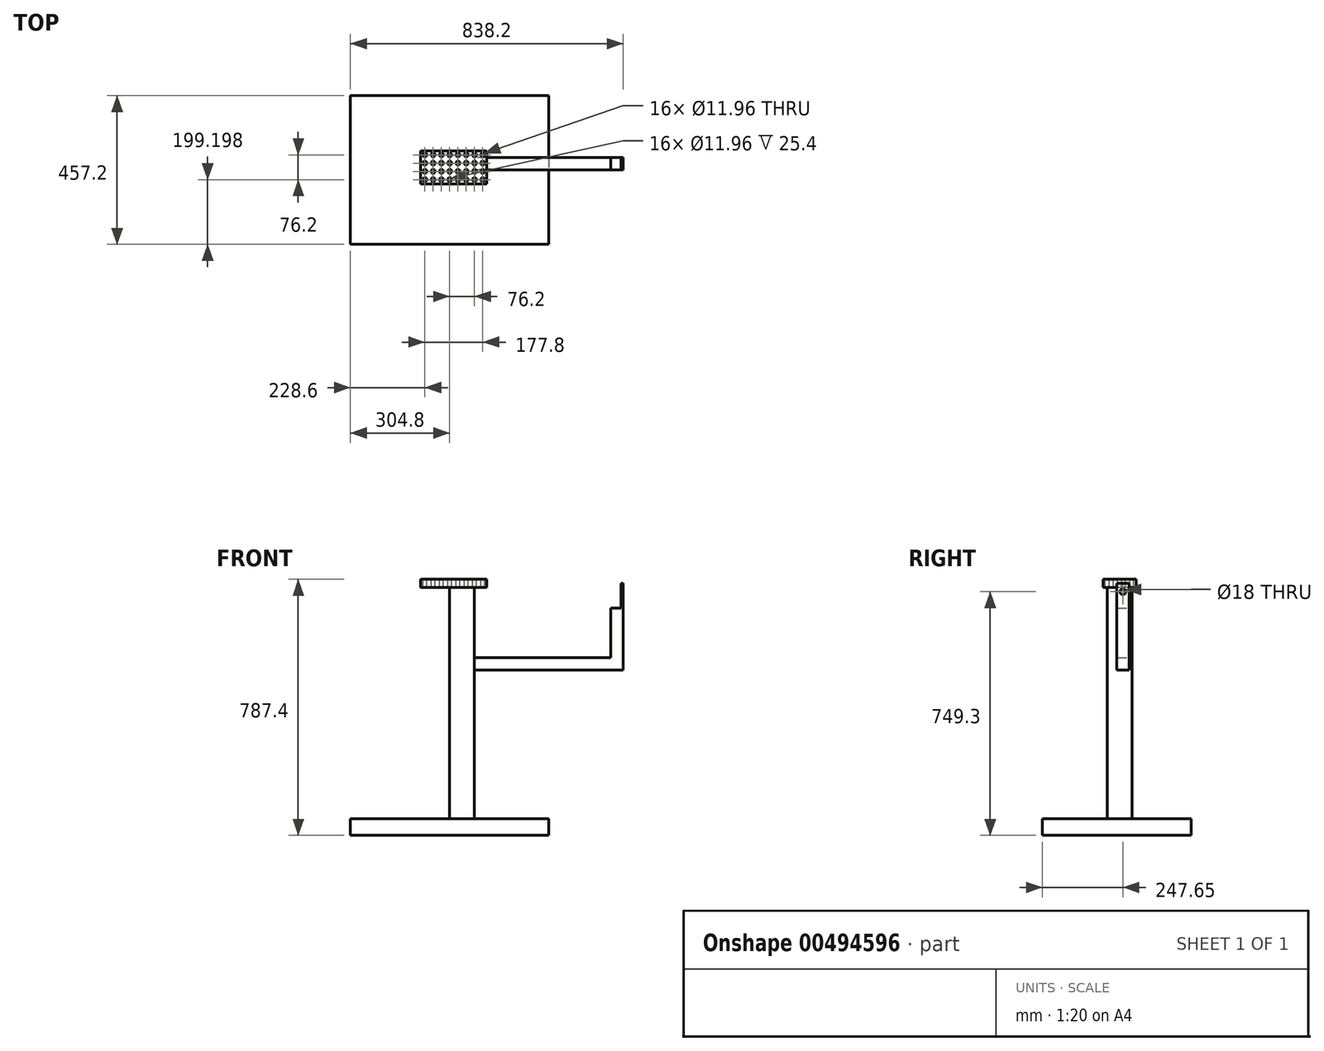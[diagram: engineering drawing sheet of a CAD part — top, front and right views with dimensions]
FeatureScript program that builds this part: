
annotation { "Feature Type Name" : "Feature", "Feature Type Description" : "" }
export const myFeature = defineFeature(function(context is Context, id is Id, definition is map)
    precondition{}
    {
        {
            var Q0;
            Q0=qCreatedBy(makeId("Top.planeOp"),FACE);
            var sketch = newSketch(context, id + "F0", { "sketchPlane" : qUnion([Q0])});
            skLineSegment(sketch, "E0.bottom", {"start": v(-304.8, 228.6) * mm, "end": v(304.8, 228.6) * mm});
            skLineSegment(sketch, "E0.top", {"start": v(-304.8, -228.6) * mm, "end": v(304.8, -228.6) * mm});
            skLineSegment(sketch, "E0.left", {"start": v(-304.8, 228.6) * mm, "end": v(-304.8, -228.6) * mm});
            skLineSegment(sketch, "E0.right", {"start": v(304.8, 228.6) * mm, "end": v(304.8, -228.6) * mm});
            skSolve(sketch);
        }
        {
            var Q0;
            Q0 = qSketchRegion(id + "F0", true);
            extrude(context, id + "F1", {"entities" : qUnion([Q0]), "depth" : 50.8 * mm});
        }
        {
            var Q0;
            Q0=makeQuery(id+"F1.opExtrude","CAP_FACE",FACE,{"disambiguationData":[OSD([sQuery(id+"F0.wireOp",EDGE,"E0.bottom"),sQuery(id+"F0.wireOp",EDGE,"E0.top"),sQuery(id+"F0.wireOp",EDGE,"E0.left"),sQuery(id+"F0.wireOp",EDGE,"E0.right")])],"isStart":false});
            var sketch = newSketch(context, id + "F2", { "sketchPlane" : qUnion([Q0])});
            skLineSegment(sketch, "E1.bottom", {"start": v(0, 46.8) * mm, "end": v(76.2, 46.8) * mm});
            skLineSegment(sketch, "E1.top", {"start": v(0, -29.4) * mm, "end": v(76.2, -29.4) * mm});
            skLineSegment(sketch, "E1.left", {"start": v(0, 46.8) * mm, "end": v(0, -29.4) * mm});
            skLineSegment(sketch, "E1.right", {"start": v(76.2, 46.8) * mm, "end": v(76.2, -29.4) * mm});
            skSolve(sketch);
        }
        {
            var Q0;
            Q0 = qSketchRegion(id + "F2", true);
            extrude(context, id + "F3", {"entities" : qUnion([Q0]), "operationType" : NewBodyOperationType.ADD, "depth" : 711.2 * mm});
        }
        {
            var Q0;
            Q0=makeQuery(id+"F3.opExtrude","CAP_FACE",FACE,{"disambiguationData":[OSD([sQuery(id+"F2.wireOp",EDGE,"E1.bottom"),sQuery(id+"F2.wireOp",EDGE,"E1.top"),sQuery(id+"F2.wireOp",EDGE,"E1.left"),sQuery(id+"F2.wireOp",EDGE,"E1.right")])],"isStart":false});
            var sketch = newSketch(context, id + "F4", { "sketchPlane" : qUnion([Q0])});
            skLineSegment(sketch, "E2.bottom", {"start": v(-88.9, 59.5) * mm, "end": v(114.3, 59.5) * mm});
            skLineSegment(sketch, "E2.top", {"start": v(-88.9, -42.1) * mm, "end": v(114.3, -42.1) * mm});
            skLineSegment(sketch, "E2.left", {"start": v(-88.9, 59.5) * mm, "end": v(-88.9, -42.1) * mm});
            skLineSegment(sketch, "E2.right", {"start": v(114.3, 59.5) * mm, "end": v(114.3, -42.1) * mm});
            skSolve(sketch);
        }
        {
            var Q0;
            Q0 = qSketchRegion(id + "F4", true);
            extrude(context, id + "F5", {"entities" : qUnion([Q0]), "operationType" : NewBodyOperationType.ADD, "depth" : 25.4 * mm});
        }
        {
            var Q0;
            Q0=makeQuery(id+"F5.opExtrude","CAP_FACE",FACE,{"disambiguationData":[OSD([sQuery(id+"F4.wireOp",EDGE,"E2.bottom"),sQuery(id+"F4.wireOp",EDGE,"E2.top"),sQuery(id+"F4.wireOp",EDGE,"E2.left"),sQuery(id+"F4.wireOp",EDGE,"E2.right")])],"isStart":false});
            var sketch = newSketch(context, id + "F6", { "sketchPlane" : qUnion([Q0])});
            skCircle(sketch, "E3", {"center": v(-76.2, 46.8) * mm, "radius": 5.98 * mm});
            skCircle(sketch, "E4.0.1.0", {"center": v(-76.2, 21.4) * mm, "radius": 5.98 * mm});
            skCircle(sketch, "E4.0.2.0", {"center": v(-76.2, -4) * mm, "radius": 5.98 * mm});
            skCircle(sketch, "E4.0.3.0", {"center": v(-76.2, -29.4) * mm, "radius": 5.98 * mm});
            skCircle(sketch, "E4.1.0.0", {"center": v(-50.8, 46.8) * mm, "radius": 5.98 * mm});
            skCircle(sketch, "E4.1.1.0", {"center": v(-50.8, 21.4) * mm, "radius": 5.98 * mm});
            skCircle(sketch, "E4.1.2.0", {"center": v(-50.8, -4) * mm, "radius": 5.98 * mm});
            skCircle(sketch, "E4.1.3.0", {"center": v(-50.8, -29.4) * mm, "radius": 5.98 * mm});
            skCircle(sketch, "E4.2.0.0", {"center": v(-25.4, 46.8) * mm, "radius": 5.98 * mm});
            skCircle(sketch, "E4.2.1.0", {"center": v(-25.4, 21.4) * mm, "radius": 5.98 * mm});
            skCircle(sketch, "E4.2.2.0", {"center": v(-25.4, -4) * mm, "radius": 5.98 * mm});
            skCircle(sketch, "E4.2.3.0", {"center": v(-25.4, -29.4) * mm, "radius": 5.98 * mm});
            skCircle(sketch, "E4.3.0.0", {"center": v(0, 46.8) * mm, "radius": 5.98 * mm});
            skCircle(sketch, "E4.3.1.0", {"center": v(0, 21.4) * mm, "radius": 5.98 * mm});
            skCircle(sketch, "E4.3.2.0", {"center": v(0, -4) * mm, "radius": 5.98 * mm});
            skCircle(sketch, "E4.3.3.0", {"center": v(0, -29.4) * mm, "radius": 5.98 * mm});
            skCircle(sketch, "E4.4.0.0", {"center": v(25.4, 46.8) * mm, "radius": 5.98 * mm});
            skCircle(sketch, "E4.4.1.0", {"center": v(25.4, 21.4) * mm, "radius": 5.98 * mm});
            skCircle(sketch, "E4.4.2.0", {"center": v(25.4, -4) * mm, "radius": 5.98 * mm});
            skCircle(sketch, "E4.4.3.0", {"center": v(25.4, -29.4) * mm, "radius": 5.98 * mm});
            skCircle(sketch, "E4.5.0.0", {"center": v(50.8, 46.8) * mm, "radius": 5.98 * mm});
            skCircle(sketch, "E4.5.1.0", {"center": v(50.8, 21.4) * mm, "radius": 5.98 * mm});
            skCircle(sketch, "E4.5.2.0", {"center": v(50.8, -4) * mm, "radius": 5.98 * mm});
            skCircle(sketch, "E4.5.3.0", {"center": v(50.8, -29.4) * mm, "radius": 5.98 * mm});
            skCircle(sketch, "E4.6.0.0", {"center": v(76.2, 46.8) * mm, "radius": 5.98 * mm});
            skCircle(sketch, "E4.6.1.0", {"center": v(76.2, 21.4) * mm, "radius": 5.98 * mm});
            skCircle(sketch, "E4.6.2.0", {"center": v(76.2, -4) * mm, "radius": 5.98 * mm});
            skCircle(sketch, "E4.6.3.0", {"center": v(76.2, -29.4) * mm, "radius": 5.98 * mm});
            skCircle(sketch, "E4.7.0.0", {"center": v(101.6, 46.8) * mm, "radius": 5.98 * mm});
            skCircle(sketch, "E4.7.1.0", {"center": v(101.6, 21.4) * mm, "radius": 5.98 * mm});
            skCircle(sketch, "E4.7.2.0", {"center": v(101.6, -4) * mm, "radius": 5.98 * mm});
            skCircle(sketch, "E4.7.3.0", {"center": v(101.6, -29.4) * mm, "radius": 5.98 * mm});
            skLineSegment(sketch, "E4.direction1", {"start": v(-76.2, 46.8) * mm, "end": v(-50.8, 46.8) * mm, "construction": true});
            skLineSegment(sketch, "E4.direction2", {"start": v(-76.2, 46.8) * mm, "end": v(-76.2, 21.4) * mm, "construction": true});
            skSolve(sketch);
        }
        {
            var Q0;
            Q0 = qSketchRegion(id + "F6", true);
            extrude(context, id + "F7", {"entities" : qUnion([Q0]), "operationType" : NewBodyOperationType.REMOVE, "oppositeDirection" : true, "depth" : 25.4 * mm});
        }
        {
            var Q0;
            Q0=makeQuery(id+"F3.opExtrude","SWEPT_FACE",FACE,{"disambiguationData":[OSD([sQuery(id+"F2.wireOp",EDGE,"E1.right")])]});
            var sketch = newSketch(context, id + "F8", { "sketchPlane" : qUnion([Q0])});
            skLineSegment(sketch, "E5.bottom", {"start": v(0, 546.1) * mm, "end": v(38.1, 546.1) * mm});
            skLineSegment(sketch, "E5.top", {"start": v(0, 508) * mm, "end": v(38.1, 508) * mm});
            skLineSegment(sketch, "E5.left", {"start": v(0, 546.1) * mm, "end": v(0, 508) * mm});
            skLineSegment(sketch, "E5.right", {"start": v(38.1, 546.1) * mm, "end": v(38.1, 508) * mm});
            skSolve(sketch);
        }
        {
            var Q0;
            Q0 = qSketchRegion(id + "F8", true);
            extrude(context, id + "F9", {"entities" : qUnion([Q0]), "operationType" : NewBodyOperationType.ADD, "depth" : 457.2 * mm});
        }
        {
            var Q0;
            Q0=makeQuery(id+"F9.opExtrude","SWEPT_FACE",FACE,{"disambiguationData":[OSD([sQuery(id+"F8.wireOp",EDGE,"E5.bottom")])]});
            var sketch = newSketch(context, id + "F10", { "sketchPlane" : qUnion([Q0])});
            skLineSegment(sketch, "E6.bottom", {"start": v(533.4, 0) * mm, "end": v(495.3, 0) * mm});
            skLineSegment(sketch, "E6.top", {"start": v(533.4, 38.1) * mm, "end": v(495.3, 38.1) * mm});
            skLineSegment(sketch, "E6.left", {"start": v(533.4, 0) * mm, "end": v(533.4, 38.1) * mm});
            skLineSegment(sketch, "E6.right", {"start": v(495.3, 0) * mm, "end": v(495.3, 38.1) * mm});
            skSolve(sketch);
        }
        {
            var Q0;
            Q0 = qSketchRegion(id + "F10", true);
            extrude(context, id + "F11", {"entities" : qUnion([Q0]), "operationType" : NewBodyOperationType.ADD, "depth" : 152.4 * mm});
        }
        {
            var Q0;
            Q0=makeQuery(id+"F11.opExtrude","CAP_FACE",FACE,{"disambiguationData":[OSD([sQuery(id+"F10.wireOp",EDGE,"E6.bottom"),sQuery(id+"F10.wireOp",EDGE,"E6.top"),sQuery(id+"F10.wireOp",EDGE,"E6.left"),sQuery(id+"F10.wireOp",EDGE,"E6.right")])],"isStart":false});
            var sketch = newSketch(context, id + "F12", { "sketchPlane" : qUnion([Q0])});
            skLineSegment(sketch, "E7.bottom", {"start": v(533.4, 0) * mm, "end": v(527.05, 0) * mm});
            skLineSegment(sketch, "E7.top", {"start": v(533.4, 38.1) * mm, "end": v(527.05, 38.1) * mm});
            skLineSegment(sketch, "E7.left", {"start": v(533.4, 0) * mm, "end": v(533.4, 38.1) * mm});
            skLineSegment(sketch, "E7.right", {"start": v(527.05, 0) * mm, "end": v(527.05, 38.1) * mm});
            skSolve(sketch);
        }
        {
            var Q0;
            Q0 = qSketchRegion(id + "F12", true);
            extrude(context, id + "F13", {"entities" : qUnion([Q0]), "operationType" : NewBodyOperationType.ADD, "depth" : 76.2 * mm});
        }
        {
            var Q0;
            Q0=makeQuery(id+"F13.boolean.opBoolean","MERGE",FACE,{"derivedFrom":[makeQuery(id+"F11.boolean.opBoolean","MERGE",FACE,{"derivedFrom":[makeQuery(id+"F9.opExtrude","CAP_FACE",FACE,{"disambiguationData":[OSD([sQuery(id+"F8.wireOp",EDGE,"E5.bottom"),sQuery(id+"F8.wireOp",EDGE,"E5.top"),sQuery(id+"F8.wireOp",EDGE,"E5.left"),sQuery(id+"F8.wireOp",EDGE,"E5.right")])],"isStart":false}),makeQuery(id+"F11.opExtrude","SWEPT_FACE",FACE,{"disambiguationData":[OSD([sQuery(id+"F10.wireOp",EDGE,"E6.left")])]})]}),makeQuery(id+"F13.opExtrude","SWEPT_FACE",FACE,{"disambiguationData":[OSD([sQuery(id+"F12.wireOp",EDGE,"E7.left")])]})]});
            var sketch = newSketch(context, id + "F14", { "sketchPlane" : qUnion([Q0])});
            skCircle(sketch, "E8", {"center": v(19.05, 749.3) * mm, "radius": 9 * mm});
            skSolve(sketch);
        }
        {
            var Q0;
            Q0 = qSketchRegion(id + "F14", true);
            extrude(context, id + "F15", {"entities" : qUnion([Q0]), "operationType" : NewBodyOperationType.REMOVE, "oppositeDirection" : true, "depth" : 25.4 * mm});
        }
    });
